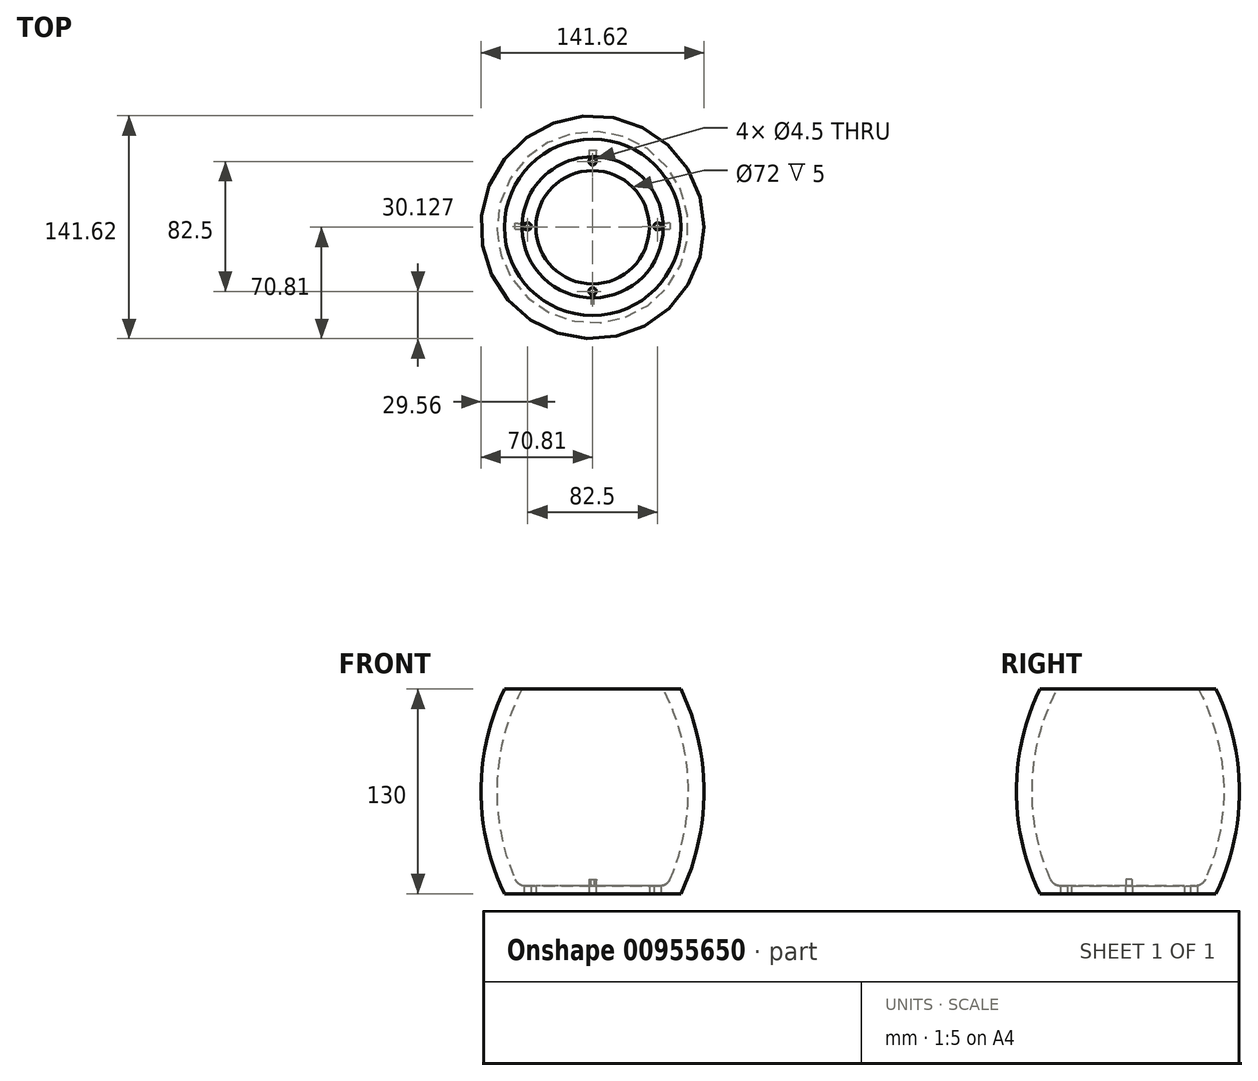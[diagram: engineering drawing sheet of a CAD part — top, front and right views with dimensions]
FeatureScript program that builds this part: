
annotation { "Feature Type Name" : "Feature", "Feature Type Description" : "" }
export const myFeature = defineFeature(function(context is Context, id is Id, definition is map)
    precondition{}
    {
        {
            var Q0;
            Q0=qCreatedBy(makeId("Top.planeOp"),FACE);
            var sketch = newSketch(context, id + "F0", { "sketchPlane" : qUnion([Q0])});
            skCircle(sketch, "E0", {"center": v(0, 0) * mm, "radius": 36 * mm});
            skCircle(sketch, "E1.0", {"center": v(0, 0) * mm, "radius": 56 * mm});
            skCircle(sketch, "E2", {"center": v(0, 41.82) * mm, "radius": 2.25 * mm});
            skCircle(sketch, "E3.1.0", {"center": v(-41.25, 0.57) * mm, "radius": 2.25 * mm});
            skCircle(sketch, "E3.2.0", {"center": v(0, -40.68) * mm, "radius": 2.25 * mm});
            skCircle(sketch, "E3.3.0", {"center": v(41.25, 0.57) * mm, "radius": 2.25 * mm});
            skPoint(sketch, "E3.center", {"position": v(0, 0.57) * mm});
            skSolve(sketch);
        }
        {
            var Q0;
            Q0=qCreatedBy(makeId("Front.planeOp"),FACE);
            var sketch = newSketch(context, id + "F1", { "sketchPlane" : qUnion([Q0])});
            skLineSegment(sketch, "E4", {"start": v(0, 0) * mm, "end": v(56, 0) * mm});
            skLineSegment(sketch, "E5", {"start": v(56, 0) * mm, "end": v(56, 130) * mm, "construction": true});
            skArc(sketch, "E6", {"start": v(56, 0) * mm, "mid": v(70.81, 65) * mm, "end": v(56, 130) * mm});
            skLineSegment(sketch, "E7", {"start": v(56, 130) * mm, "end": v(0, 130) * mm});
            skLineSegment(sketch, "E8", {"start": v(0, 130) * mm, "end": v(0, 0) * mm});
            skLineSegment(sketch, "E9", {"start": v(36, 0) * mm, "end": v(36, 130) * mm, "construction": true});
            skArc(sketch, "E10.0", {"start": v(44.81, 0) * mm, "mid": v(60.81, 65) * mm, "end": v(44.81, 130) * mm});
            skSolve(sketch);
        }
        {
            var Q0;
            {var subQ0=sQuery(id+"F1.wireOp",EDGE,"E6");Q0=makeQuery(id+"F1.imprint","IMPRINT",FACE,{"disambiguationData":[TD([[makeQuery(id+"F1.imprint","IMPRINT",EDGE,{"derivedFrom":subQ0}),1.0]])]});}
            var Q1;
            Q1=sQuery(id+"F1.wireOp",EDGE,"E8");
            revolve(context, id + "F2", {"surfaceOperationType" : NewSurfaceOperationType.NEW, "entities" : qUnion([Q0]), "axis" : qUnion([Q1]), "revolveType" : RevolveType.FULL});
        }
        {
            var Q0;
            Q0=makeQuery(id+"F0.imprint","IMPRINT",FACE,{"disambiguationData":[TD([[makeQuery(id+"F0.imprint","IMPRINT",EDGE,{"derivedFrom":sQuery(id+"F0.wireOp",EDGE,"E0")}),-1.0]])]});
            extrude(context, id + "F3", {"entities" : qUnion([Q0]), "operationType" : NewBodyOperationType.ADD, "depth" : 5 * mm, "offsetDistance" : 25 * mm});
        }
        {
            var Q0;
            Q0=makeQuery(id+"F3.boolean.opBoolean","INTERSECT",EDGE,{"derivedFrom":[makeQuery(id+"F2.opRevolve","SWEPT_FACE",FACE,{"disambiguationData":[OSD([sQuery(id+"F1.wireOp",EDGE,"E10.0")])]}),makeQuery(id+"F3.opExtrude","CAP_FACE",FACE,{"disambiguationData":[OSD([sQuery(id+"F0.wireOp",EDGE,"E0"),sQuery(id+"F0.wireOp",EDGE,"E1.0"),sQuery(id+"F0.wireOp",EDGE,"E2"),sQuery(id+"F0.wireOp",EDGE,"E3.1.0"),sQuery(id+"F0.wireOp",EDGE,"E3.2.0"),sQuery(id+"F0.wireOp",EDGE,"E3.3.0")])],"isStart":false})]});
            fillet(context, id + "F4", {"entities" : qUnion([Q0]), "radius" : 7 * mm, "tangentPropagation" : true, "allowEdgeOverflow" : false});
        }
    });
